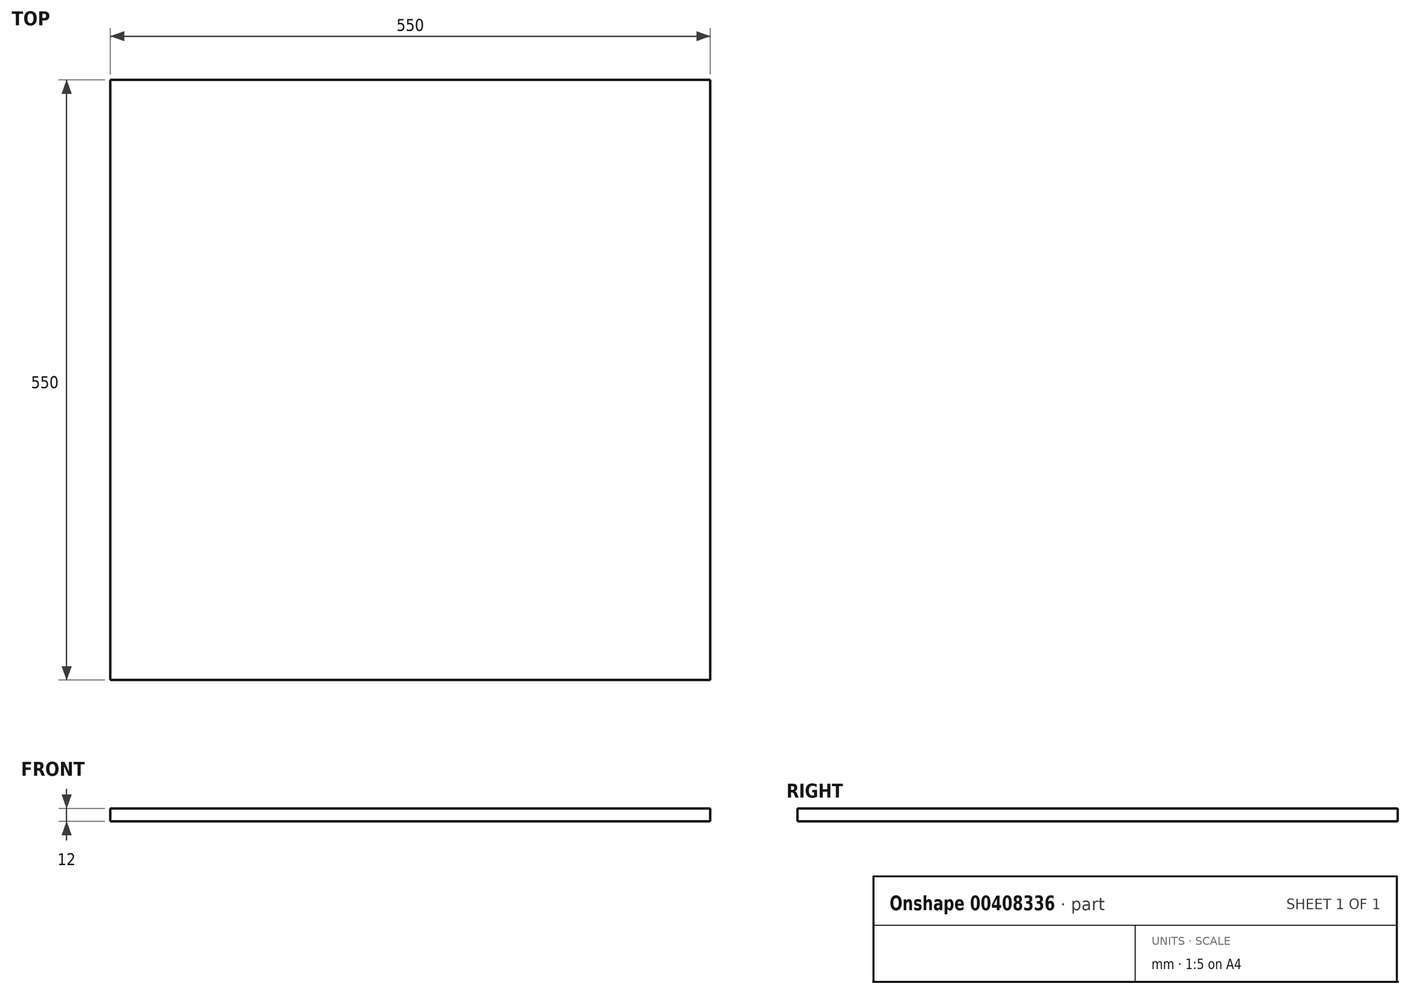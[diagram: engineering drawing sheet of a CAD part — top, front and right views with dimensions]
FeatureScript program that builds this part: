
annotation { "Feature Type Name" : "Feature", "Feature Type Description" : "" }
export const myFeature = defineFeature(function(context is Context, id is Id, definition is map)
    precondition{}
    {
        {
            var Q0;
            Q0=qCreatedBy(makeId("Top.planeOp"),FACE);
            var sketch = newSketch(context, id + "F0", { "sketchPlane" : qUnion([Q0])});
            skLineSegment(sketch, "E0.bottom", {"start": v(275, 275) * mm, "end": v(-275, 275) * mm});
            skLineSegment(sketch, "E0.top", {"start": v(275, -275) * mm, "end": v(-275, -275) * mm});
            skLineSegment(sketch, "E0.left", {"start": v(275, 275) * mm, "end": v(275, -275) * mm});
            skLineSegment(sketch, "E0.right", {"start": v(-275, 275) * mm, "end": v(-275, -275) * mm});
            skPoint(sketch, "E0.middle", {"position": v(0, 0) * mm});
            skSolve(sketch);
        }
        {
            var Q0;
            Q0=makeQuery(id+"F0.imprint","IMPRINT",FACE,{"disambiguationData":[TD([[makeQuery(id+"F0.imprint","IMPRINT",EDGE,{"derivedFrom":sQuery(id+"F0.wireOp",EDGE,"E0.bottom")}),1.0]])]});
            extrude(context, id + "F1", {"entities" : qUnion([Q0]), "depth" : 12 * mm});
        }
    });
